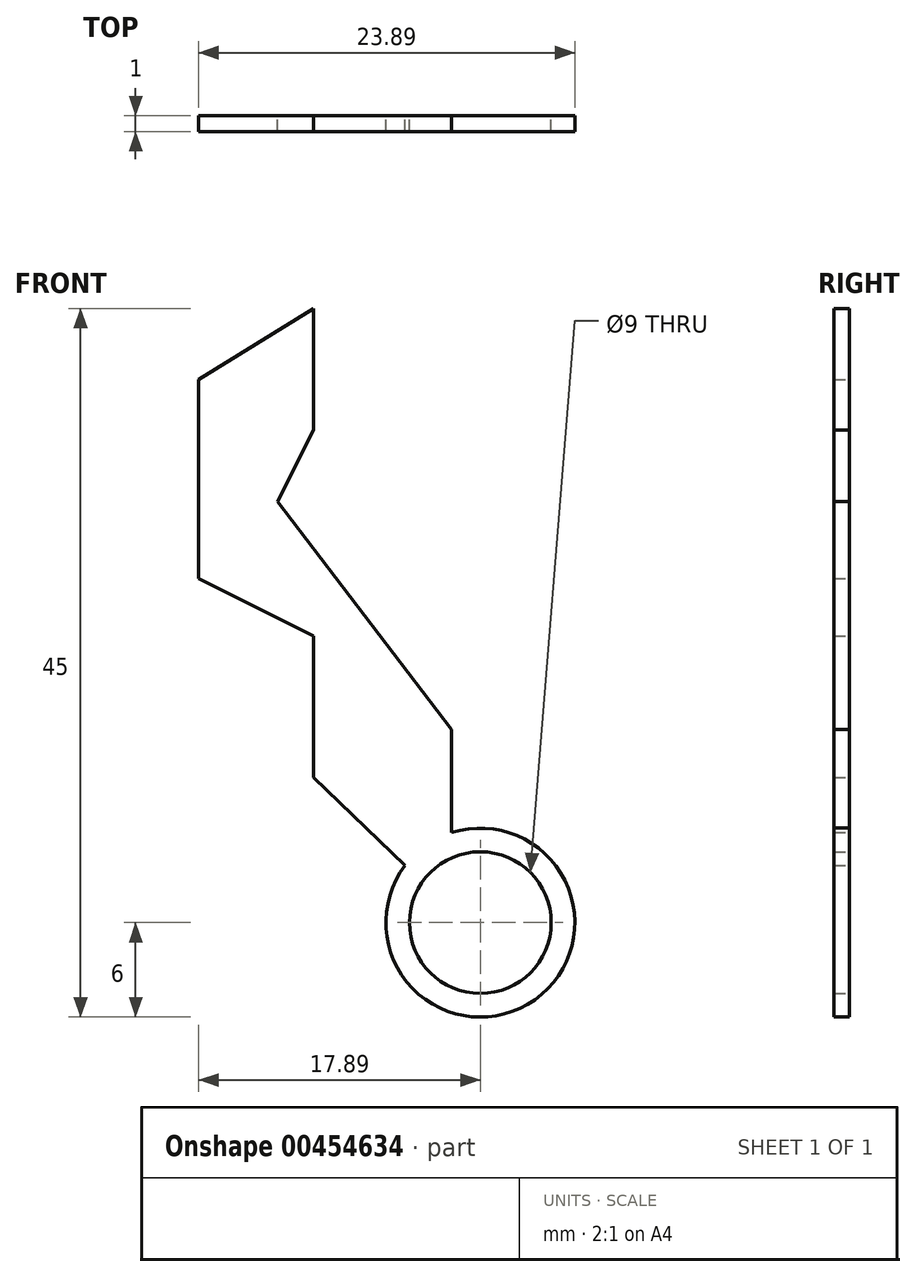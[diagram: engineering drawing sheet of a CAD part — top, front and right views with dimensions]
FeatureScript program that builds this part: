
annotation { "Feature Type Name" : "Feature", "Feature Type Description" : "" }
export const myFeature = defineFeature(function(context is Context, id is Id, definition is map)
    precondition{}
    {
        {
            var Q0;
            Q0=qCreatedBy(makeId("Front.planeOp"),FACE);
            var sketch = newSketch(context, id + "F0", { "sketchPlane" : qUnion([Q0])});
            skCircle(sketch, "E0", {"center": v(0, 0) * mm, "radius": 4.5 * mm});
            skArc(sketch, "E1", {"start": v(-4.78, 3.63) * mm, "mid": v(3.46, -4.9) * mm, "end": v(-1.82, 5.72) * mm});
            skLineSegment(sketch, "E2", {"start": v(-4.78, 3.63) * mm, "end": v(-10.6, 9.21) * mm});
            skLineSegment(sketch, "E3", {"start": v(-10.6, 9.21) * mm, "end": v(-10.6, 18.21) * mm});
            skLineSegment(sketch, "E4", {"start": v(-10.6, 18.21) * mm, "end": v(-17.9, 21.86) * mm});
            skLineSegment(sketch, "E5", {"start": v(-17.9, 21.86) * mm, "end": v(-17.9, 34.5) * mm});
            skLineSegment(sketch, "E6", {"start": v(-17.9, 34.5) * mm, "end": v(-10.6, 39) * mm});
            skLineSegment(sketch, "E7", {"start": v(-10.6, 39) * mm, "end": v(-10.6, 31.29) * mm});
            skLineSegment(sketch, "E8", {"start": v(-10.6, 31.29) * mm, "end": v(-12.88, 26.74) * mm});
            skLineSegment(sketch, "E9", {"start": v(-12.88, 26.74) * mm, "end": v(-9.15, 21.86) * mm});
            skLineSegment(sketch, "E10", {"start": v(-9.15, 21.86) * mm, "end": v(-1.82, 12.27) * mm});
            skLineSegment(sketch, "E11", {"start": v(-1.82, 12.27) * mm, "end": v(-1.82, 5.72) * mm});
            skSolve(sketch);
        }
        {
            var Q0;
            Q0 = qSketchRegion(id + "F0", true);
            extrude(context, id + "F1", {"entities" : qUnion([Q0]), "depth" : 1 * mm});
        }
    });
